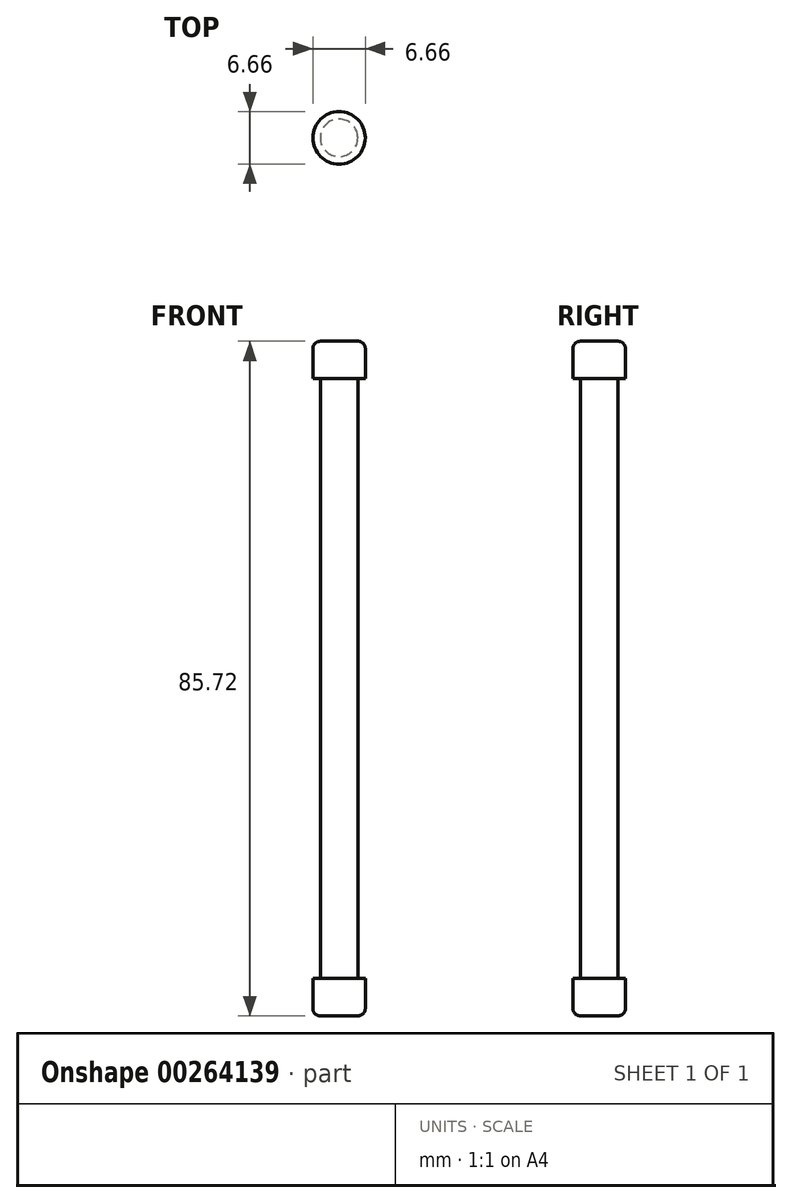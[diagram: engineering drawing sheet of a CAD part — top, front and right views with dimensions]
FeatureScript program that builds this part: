
annotation { "Feature Type Name" : "Feature", "Feature Type Description" : "" }
export const myFeature = defineFeature(function(context is Context, id is Id, definition is map)
    precondition{}
    {
        {
            var Q0;
            Q0=qCreatedBy(makeId("Top.planeOp"),FACE);
            var sketch = newSketch(context, id + "F0", { "sketchPlane" : qUnion([Q0])});
            skCircle(sketch, "E0", {"center": v(0, 0) * mm, "radius": 2.38 * mm});
            skSolve(sketch);
        }
        {
            var Q0;
            Q0 = qSketchRegion(id + "F0", true);
            extrude(context, id + "F1", {"entities" : qUnion([Q0]), "depth" : 76.2 * mm});
        }
        {
            var Q0;
            Q0=makeQuery(id+"F1.opExtrude","CAP_FACE",FACE,{"disambiguationData":[OSD([sQuery(id+"F0.wireOp",EDGE,"E0")])],"isStart":false});
            var sketch = newSketch(context, id + "F2", { "sketchPlane" : qUnion([Q0])});
            skCircle(sketch, "E1", {"center": v(0, 0) * mm, "radius": 3.33 * mm});
            skSolve(sketch);
        }
        {
            var Q0;
            Q0 = qSketchRegion(id + "F2", true);
            extrude(context, id + "F3", {"entities" : qUnion([Q0]), "operationType" : NewBodyOperationType.ADD, "depth" : 4.76 * mm});
        }
        {
            var Q0;
            Q0=makeQuery(id+"F1.opExtrude","CAP_FACE",FACE,{"disambiguationData":[OSD([sQuery(id+"F0.wireOp",EDGE,"E0")])],"isStart":true});
            var sketch = newSketch(context, id + "F4", { "sketchPlane" : qUnion([Q0])});
            skCircle(sketch, "E2", {"center": v(0, 0) * mm, "radius": 3.33 * mm});
            skSolve(sketch);
        }
        {
            var Q0;
            Q0 = qSketchRegion(id + "F4", true);
            extrude(context, id + "F5", {"entities" : qUnion([Q0]), "operationType" : NewBodyOperationType.ADD, "depth" : 4.76 * mm});
        }
        {
            var Q0;
            Q0=makeQuery(id+"F3.opExtrude","CAP_EDGE",EDGE,{"disambiguationData":[OSD([sQuery(id+"F2.wireOp",EDGE,"E1")])],"isStart":false});
            var Q1;
            Q1=makeQuery(id+"F5.opExtrude","CAP_EDGE",EDGE,{"disambiguationData":[OSD([sQuery(id+"F4.wireOp",EDGE,"E2")])],"isStart":false});
            fillet(context, id + "F6", {"entities" : qUnion([Q0, Q1]), "radius" : 0.95 * mm, "tangentPropagation" : true, "allowEdgeOverflow" : false});
        }
    });
